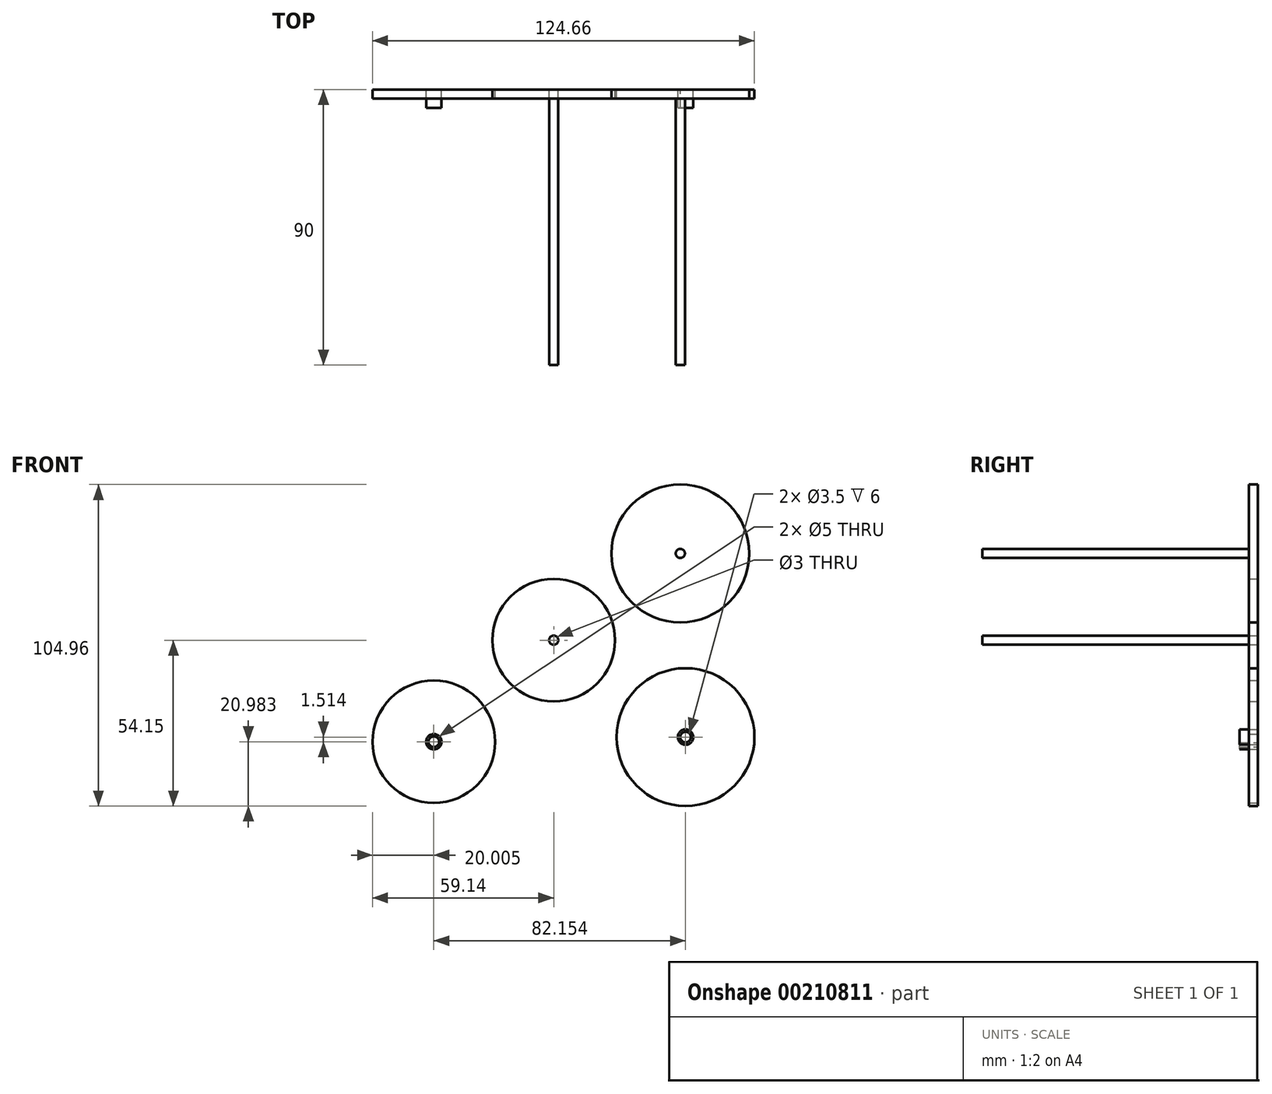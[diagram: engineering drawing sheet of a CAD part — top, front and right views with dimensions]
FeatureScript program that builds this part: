
annotation { "Feature Type Name" : "Feature", "Feature Type Description" : "" }
export const myFeature = defineFeature(function(context is Context, id is Id, definition is map)
    precondition{}
    {
        {
            var Q0;
            Q0=qCreatedBy(makeId("Front.planeOp"),FACE);
            var sketch = newSketch(context, id + "F0", { "sketchPlane" : qUnion([Q0])});
            skCircle(sketch, "E0", {"center": v(0, 0) * mm, "radius": 20 * mm});
            skCircle(sketch, "E1", {"center": v(0, 0) * mm, "radius": 1.5 * mm});
            skCircle(sketch, "E2", {"center": v(-39.14, -33.17) * mm, "radius": 20 * mm});
            skCircle(sketch, "E3", {"center": v(43.02, -31.65) * mm, "radius": 22.5 * mm});
            skCircle(sketch, "E4", {"center": v(-39.14, -33.17) * mm, "radius": 2.5 * mm});
            skCircle(sketch, "E5", {"center": v(43.02, -31.65) * mm, "radius": 2.5 * mm});
            skCircle(sketch, "E6", {"center": v(-39.14, -33.17) * mm, "radius": 1.75 * mm});
            skCircle(sketch, "E7", {"center": v(43.02, -31.65) * mm, "radius": 1.75 * mm});
            skCircle(sketch, "E8", {"center": v(41.31, 28.3) * mm, "radius": 22.5 * mm});
            skCircle(sketch, "E9", {"center": v(41.31, 28.3) * mm, "radius": 1.5 * mm});
            skSolve(sketch);
        }
        {
            var Q0;
            Q0=makeQuery(id+"F0.imprint","IMPRINT",FACE,{"disambiguationData":[TD([[makeQuery(id+"F0.imprint","IMPRINT",EDGE,{"derivedFrom":sQuery(id+"F0.wireOp",EDGE,"E0")}),1.0]])]});
            var Q1;
            Q1=makeQuery(id+"F0.imprint","IMPRINT",FACE,{"disambiguationData":[TD([[makeQuery(id+"F0.imprint","IMPRINT",EDGE,{"derivedFrom":sQuery(id+"F0.wireOp",EDGE,"E2")}),1.0]])]});
            var Q2;
            Q2=makeQuery(id+"F0.imprint","IMPRINT",FACE,{"disambiguationData":[TD([[makeQuery(id+"F0.imprint","IMPRINT",EDGE,{"derivedFrom":sQuery(id+"F0.wireOp",EDGE,"E3")}),1.0]])]});
            var Q3;
            Q3=makeQuery(id+"F0.imprint","IMPRINT",FACE,{"disambiguationData":[TD([[makeQuery(id+"F0.imprint","IMPRINT",EDGE,{"derivedFrom":sQuery(id+"F0.wireOp",EDGE,"E8")}),1.0]])]});
            extrude(context, id + "F1", {"entities" : qUnion([Q0, Q1, Q2, Q3]), "depth" : 3 * mm});
        }
        {
            var Q0;
            Q0=makeQuery(id+"F0.imprint","IMPRINT",FACE,{"disambiguationData":[TD([[makeQuery(id+"F0.imprint","IMPRINT",EDGE,{"derivedFrom":sQuery(id+"F0.wireOp",EDGE,"E1")}),1.0]])]});
            extrude(context, id + "F2", {"entities" : qUnion([Q0]), "depth" : 90 * mm});
        }
        {
            var Q0;
            Q0=makeQuery(id+"F0.imprint","IMPRINT",FACE,{"disambiguationData":[TD([[makeQuery(id+"F0.imprint","IMPRINT",EDGE,{"derivedFrom":sQuery(id+"F0.wireOp",EDGE,"E4")}),1.0]])]});
            var Q1;
            Q1=makeQuery(id+"F0.imprint","IMPRINT",FACE,{"disambiguationData":[TD([[makeQuery(id+"F0.imprint","IMPRINT",EDGE,{"derivedFrom":sQuery(id+"F0.wireOp",EDGE,"E5")}),1.0]])]});
            var Q2;
            Q2=makeQuery(id+"F0.imprint","IMPRINT",FACE,{"disambiguationData":[TD([[makeQuery(id+"F0.imprint","IMPRINT",EDGE,{"derivedFrom":sQuery(id+"F0.wireOp",EDGE,"95a3b00f-2419-4f02-8021-0434124c8d9b")}),1.0]])]});
            extrude(context, id + "F3", {"entities" : qUnion([Q0, Q1, Q2]), "depth" : 6 * mm});
        }
        {
            var Q0;
            Q0=makeQuery(id+"F0.imprint","IMPRINT",FACE,{"disambiguationData":[TD([[makeQuery(id+"F0.imprint","IMPRINT",EDGE,{"derivedFrom":sQuery(id+"F0.wireOp",EDGE,"E9")}),1.0]])]});
            extrude(context, id + "F4", {"entities" : qUnion([Q0]), "operationType" : NewBodyOperationType.ADD, "depth" : 90 * mm});
        }
    });
